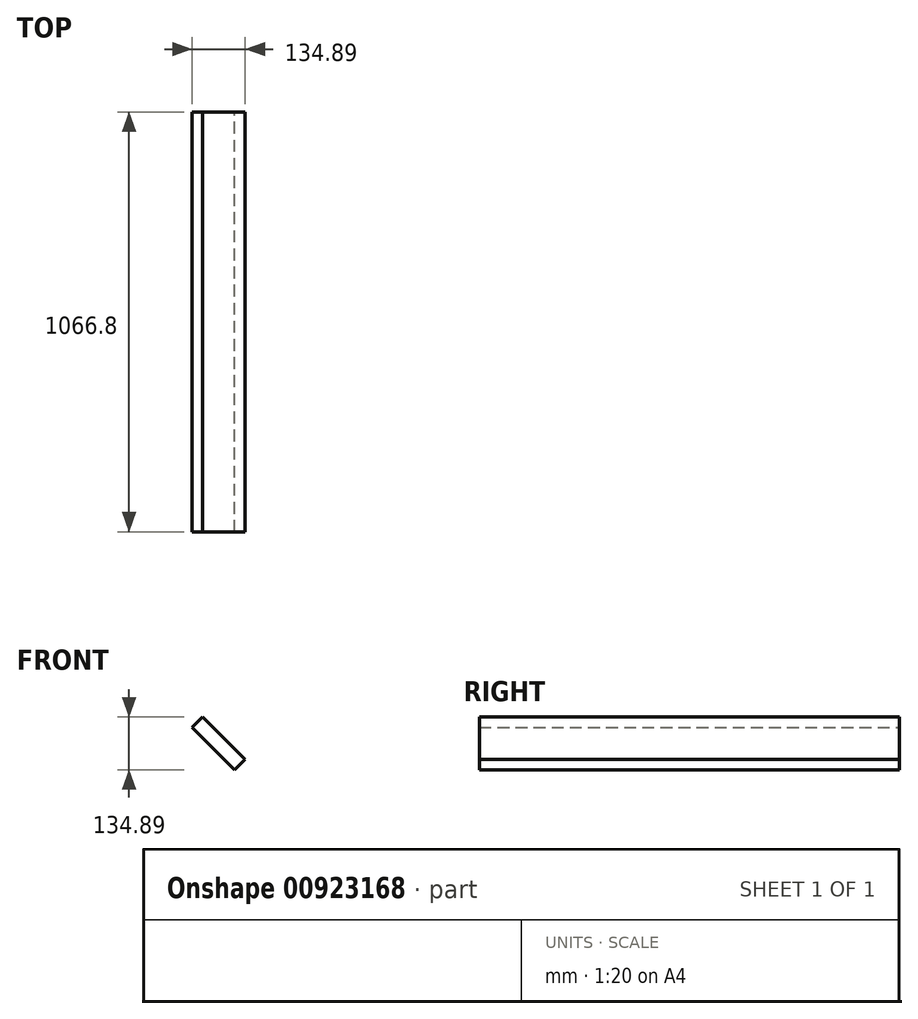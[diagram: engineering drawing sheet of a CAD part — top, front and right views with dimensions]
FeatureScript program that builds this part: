
annotation { "Feature Type Name" : "Feature", "Feature Type Description" : "" }
export const myFeature = defineFeature(function(context is Context, id is Id, definition is map)
    precondition{}
    {
        {
            var Q0;
            Q0=qCreatedBy(makeId("Front.planeOp"),FACE);
            var sketch = newSketch(context, id + "F0", { "sketchPlane" : qUnion([Q0])});
            skLineSegment(sketch, "E0", {"start": v(0, 0) * mm, "end": v(107.95, 0) * mm});
            skLineSegment(sketch, "E1", {"start": v(0, 0) * mm, "end": v(0, 107.95) * mm});
            skLineSegment(sketch, "E2", {"start": v(0, 107.95) * mm, "end": v(107.95, 0) * mm});
            skLineSegment(sketch, "E3", {"start": v(0, 107.95) * mm, "end": v(26.94, 134.9) * mm});
            skLineSegment(sketch, "E4", {"start": v(107.95, 0) * mm, "end": v(134.9, 26.94) * mm});
            skLineSegment(sketch, "E5", {"start": v(26.94, 134.9) * mm, "end": v(134.9, 26.94) * mm});
            skSolve(sketch);
        }
        {
            var Q0;
            Q0=makeQuery(id+"F0.imprint","IMPRINT",FACE,{"disambiguationData":[TD([[makeQuery(id+"F0.imprint","IMPRINT",EDGE,{"derivedFrom":sQuery(id+"F0.wireOp",EDGE,"E2")}),1.0]])]});
            extrude(context, id + "F1", {"entities" : qUnion([Q0]), "endBound" : BoundingType.SYMMETRIC, "depth" : 1066.8 * mm, "offsetDistance" : 25.4 * mm});
        }
    });
